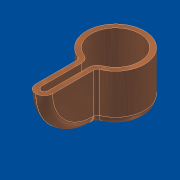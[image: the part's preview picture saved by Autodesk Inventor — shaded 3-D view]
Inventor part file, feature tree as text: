
AUTODESK INVENTOR PART (.ipt)
format: ipt  version: unknown  size: 331,776 bytes
history: native  units: mm
features: sketch x5, extrude x3, other x2, projected_geometry x2, plane x1, fillet x1, revolve x1, delete_face x1, thicken_offset x1, hole x1
ambient origin geometry x8: Origin, YZ Plane, XZ Plane, XY Plane, X Axis, Y Axis, Z Axis, Center Point
feature tree (18):
  extrude  "Extrusion1"  Depth=10.0mm TaperAngle=0.0deg
  plane  "Work Plane1"
  extrude  "Extrusion2"  Depth=10.0mm TaperAngle=0.0deg
  extrude  "Extrusion3"  Depth=3.6mm
  fillet  "Fillet1"  Radius=1.5mm
  revolve  "Revolution1"  [1 undecoded]
  delete_face  "Delete Face1"
  thicken_offset  "Thicken1"
  hole  "Hole1"  [1 undecoded]
  sketch  "Sketch1"  dims[d0=10.0mm d1=0.0mm d2=10.0mm d3=0.0mm]
  other  "Work Axis1"
  other  "Work Axis2"
  sketch  "Sketch2"  dims[d4=20.0mm d5=10.0mm d6=0.0mm]
  sketch  "Sketch3"  dims[d7=1.74mm d8=3.6mm d9=1.5mm]
  projected_geometry  "Projected Loop1"
  projected_geometry  "Projected Loop2"
  sketch  "Sketch4"  dims[d10=90.0deg d11=1.0mm]
  sketch  "Sketch5"  dims[d12=2.0mm d13=6.0mm d14=4.0mm d15=2.0mm d16=90.0deg d17=8.0mm d18=20.594885mm]
note: 2 required parameter values undecoded (feature->parameter linkage not recoverable at this tier; creation-order binding heuristic only, values carry confidence <= 0.55)